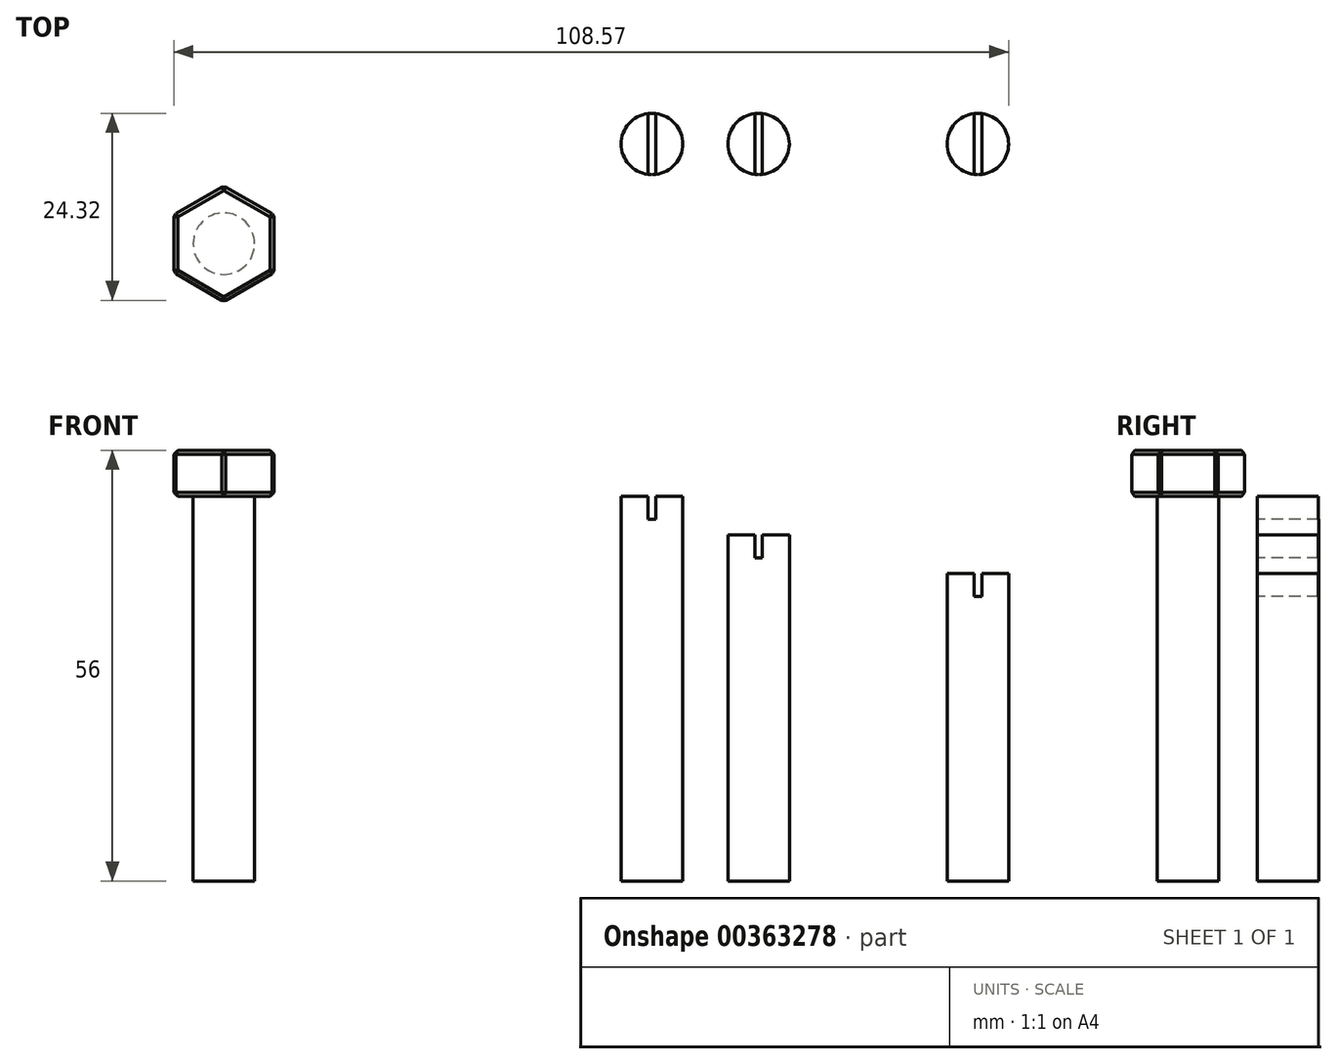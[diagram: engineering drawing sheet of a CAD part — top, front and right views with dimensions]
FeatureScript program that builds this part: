
annotation { "Feature Type Name" : "Feature", "Feature Type Description" : "" }
export const myFeature = defineFeature(function(context is Context, id is Id, definition is map)
    precondition{}
    {
        {
            var Q0;
            Q0=qCreatedBy(makeId("Top.planeOp"),FACE);
            var sketch = newSketch(context, id + "F0", { "sketchPlane" : qUnion([Q0])});
            skCircle(sketch, "E0", {"center": v(0, 0) * mm, "radius": 4 * mm});
            skSolve(sketch);
        }
        {
            var Q0;
            Q0=qSketchRegion(id+"F0",true);
            extrude(context, id + "F1", {"entities" : qUnion([Q0]), "depth" : 50 * mm});
        }
        {
            var Q0;
            Q0=qCreatedBy(makeId("Top.planeOp"),FACE);
            var sketch = newSketch(context, id + "F2", { "sketchPlane" : qUnion([Q0])});
            skCircle(sketch, "E1", {"center": v(42.4, 0) * mm, "radius": 4 * mm});
            skSolve(sketch);
        }
        {
            var Q0;
            Q0=makeQuery(id+"F2.imprint","IMPRINT",FACE,{"disambiguationData":[TD([[makeQuery(id+"F2.imprint","IMPRINT",EDGE,{"derivedFrom":sQuery(id+"F2.wireOp",EDGE,"E1")}),1.0]])]});
            var Q1;
            Q1=sQuery(id+"F2.wireOp",EDGE,"E1");
            extrude(context, id + "F3", {"entities" : qUnion([Q0]), "surfaceEntities" : qUnion([Q1]), "depth" : 40 * mm});
        }
        {
            var Q0;
            Q0=makeQuery(id+"F1.opExtrude","CAP_FACE",FACE,{"disambiguationData":[OSD([sQuery(id+"F0.wireOp",EDGE,"E0")])],"isStart":false});
            var sketch = newSketch(context, id + "F4", { "sketchPlane" : qUnion([Q0])});
            skLineSegment(sketch, "E2.bottom", {"start": v(0.5, 4) * mm, "end": v(-0.5, 4) * mm});
            skLineSegment(sketch, "E2.top", {"start": v(0.5, -4) * mm, "end": v(-0.5, -4) * mm});
            skLineSegment(sketch, "E2.left", {"start": v(0.5, 4) * mm, "end": v(0.5, -4) * mm});
            skLineSegment(sketch, "E2.right", {"start": v(-0.5, 4) * mm, "end": v(-0.5, -4) * mm});
            skPoint(sketch, "E2.middle", {"position": v(0, 0) * mm});
            skSolve(sketch);
        }
        {
            var Q0;
            {var subQ0=makeQuery(id+"F1.opExtrude","CAP_EDGE",EDGE,{"disambiguationData":[OSD([sQuery(id+"F0.wireOp",EDGE,"E0")])],"isStart":false});var subQ4=sQuery(id+"F4.wireOp",EDGE,"E2.left");var subQ5=makeQuery(id+"F4.imprint","INTERSECT",VERTEX,{"disambiguationData":[OD(0.0)],"derivedFrom":[subQ0,subQ4]});Q0=makeQuery(id+"F4.imprint","IMPRINT",FACE,{"disambiguationData":[TD([[makeQuery(id+"F4.imprint","IMPRINT",EDGE,{"disambiguationData":[TD([[subQ5,-1.0]])],"derivedFrom":subQ4}),-1.0]])]});}
            extrude(context, id + "F5", {"entities" : qUnion([Q0]), "operationType" : NewBodyOperationType.REMOVE, "oppositeDirection" : true, "depth" : 3 * mm});
        }
        {
            var Q0;
            Q0=makeQuery(id+"F3.opExtrude","CAP_FACE",FACE,{"disambiguationData":[OSD([sQuery(id+"F2.wireOp",EDGE,"E1")])],"isStart":false});
            var sketch = newSketch(context, id + "F6", { "sketchPlane" : qUnion([Q0])});
            skLineSegment(sketch, "E3.bottom", {"start": v(42.9, 4) * mm, "end": v(41.9, 4) * mm});
            skLineSegment(sketch, "E3.top", {"start": v(42.9, -4) * mm, "end": v(41.9, -4) * mm});
            skLineSegment(sketch, "E3.left", {"start": v(42.9, 4) * mm, "end": v(42.9, -4) * mm});
            skLineSegment(sketch, "E3.right", {"start": v(41.9, 4) * mm, "end": v(41.9, -4) * mm});
            skPoint(sketch, "E3.middle", {"position": v(42.4, 0) * mm});
            skSolve(sketch);
        }
        {
            var Q0;
            {var subQ0=makeQuery(id+"F3.opExtrude","CAP_EDGE",EDGE,{"disambiguationData":[OSD([sQuery(id+"F2.wireOp",EDGE,"E1")])],"isStart":false});var subQ5=sQuery(id+"F6.wireOp",EDGE,"E3.left");var subQ6=makeQuery(id+"F6.imprint","INTERSECT",VERTEX,{"disambiguationData":[OD(0.0)],"derivedFrom":[subQ0,subQ5]});Q0=makeQuery(id+"F6.imprint","IMPRINT",FACE,{"disambiguationData":[TD([[makeQuery(id+"F6.imprint","IMPRINT",EDGE,{"disambiguationData":[TD([[subQ6,-1.0]])],"derivedFrom":subQ5}),-1.0]])]});}
            extrude(context, id + "F7", {"entities" : qUnion([Q0]), "operationType" : NewBodyOperationType.REMOVE, "oppositeDirection" : true, "depth" : 3 * mm});
        }
        {
            var Q0;
            Q0=qCreatedBy(makeId("Top.planeOp"),FACE);
            var sketch = newSketch(context, id + "F8", { "sketchPlane" : qUnion([Q0])});
            skCircle(sketch, "E4", {"center": v(13.88, 0) * mm, "radius": 4 * mm});
            skSolve(sketch);
        }
        {
            var Q0;
            Q0=makeQuery(id+"F8.imprint","IMPRINT",FACE,{"disambiguationData":[TD([[makeQuery(id+"F8.imprint","IMPRINT",EDGE,{"derivedFrom":sQuery(id+"F8.wireOp",EDGE,"E4")}),1.0]])]});
            var Q1;
            Q1=sQuery(id+"F8.wireOp",EDGE,"E4");
            extrude(context, id + "F9", {"entities" : qUnion([Q0]), "surfaceEntities" : qUnion([Q1]), "depth" : 45 * mm});
        }
        {
            var Q0;
            Q0=makeQuery(id+"F9.opExtrude","CAP_FACE",FACE,{"disambiguationData":[OSD([sQuery(id+"F8.wireOp",EDGE,"E4")])],"isStart":false});
            var sketch = newSketch(context, id + "F10", { "sketchPlane" : qUnion([Q0])});
            skLineSegment(sketch, "E5.bottom", {"start": v(14.38, 4) * mm, "end": v(13.38, 4) * mm});
            skLineSegment(sketch, "E5.top", {"start": v(14.38, -4) * mm, "end": v(13.38, -4) * mm});
            skLineSegment(sketch, "E5.left", {"start": v(14.38, 4) * mm, "end": v(14.38, -4) * mm});
            skLineSegment(sketch, "E5.right", {"start": v(13.38, 4) * mm, "end": v(13.38, -4) * mm});
            skPoint(sketch, "E5.middle", {"position": v(13.88, 0) * mm});
            skSolve(sketch);
        }
        {
            var Q0;
            {var subQ0=makeQuery(id+"F9.opExtrude","CAP_EDGE",EDGE,{"disambiguationData":[OSD([sQuery(id+"F8.wireOp",EDGE,"E4")])],"isStart":false});var subQ4=sQuery(id+"F10.wireOp",EDGE,"E5.left");var subQ5=makeQuery(id+"F10.imprint","INTERSECT",VERTEX,{"disambiguationData":[OD(0.0)],"derivedFrom":[subQ0,subQ4]});Q0=makeQuery(id+"F10.imprint","IMPRINT",FACE,{"disambiguationData":[TD([[makeQuery(id+"F10.imprint","IMPRINT",EDGE,{"disambiguationData":[TD([[subQ5,-1.0]])],"derivedFrom":subQ4}),-1.0]])]});}
            extrude(context, id + "F11", {"entities" : qUnion([Q0]), "operationType" : NewBodyOperationType.REMOVE, "oppositeDirection" : true, "depth" : 3 * mm});
        }
        {
            var Q0;
            Q0=qCreatedBy(makeId("Top.planeOp"),FACE);
            var sketch = newSketch(context, id + "F12", { "sketchPlane" : qUnion([Q0])});
            skCircle(sketch, "E6", {"center": v(-55.68, -12.96) * mm, "radius": 4 * mm});
            skSolve(sketch);
        }
        {
            var Q0;
            Q0=makeQuery(id+"F12.imprint","IMPRINT",FACE,{"disambiguationData":[TD([[makeQuery(id+"F12.imprint","IMPRINT",EDGE,{"derivedFrom":sQuery(id+"F12.wireOp",EDGE,"E6")}),1.0]])]});
            extrude(context, id + "F13", {"entities" : qUnion([Q0]), "depth" : 50 * mm});
        }
        {
            var Q0;
            Q0=makeQuery(id+"F13.opExtrude","CAP_FACE",FACE,{"disambiguationData":[OSD([sQuery(id+"F12.wireOp",EDGE,"E6")])],"isStart":false});
            var sketch = newSketch(context, id + "F14", { "sketchPlane" : qUnion([Q0])});
            skCircle(sketch, "E7.cCircle", {"center": v(-55.68, -12.96) * mm, "radius": 6.5 * mm, "construction": true});
            skLineSegment(sketch, "E7.0", {"start": v(-49.18, -9.2) * mm, "end": v(-49.18, -16.72) * mm});
            skLineSegment(sketch, "E7.1", {"start": v(-49.18, -16.72) * mm, "end": v(-55.68, -20.47) * mm});
            skLineSegment(sketch, "E7.2", {"start": v(-55.68, -20.47) * mm, "end": v(-62.18, -16.72) * mm});
            skLineSegment(sketch, "E7.3", {"start": v(-62.18, -16.72) * mm, "end": v(-62.18, -9.2) * mm});
            skLineSegment(sketch, "E7.4", {"start": v(-62.18, -9.2) * mm, "end": v(-55.68, -5.46) * mm});
            skLineSegment(sketch, "E7.5", {"start": v(-55.68, -5.46) * mm, "end": v(-49.18, -9.2) * mm});
            skPoint(sketch, "E7.0.midPoint", {"position": v(-49.18, -12.96) * mm});
            skSolve(sketch);
        }
        {
            var Q0;
            Q0=qSketchRegion(id+"F14",true);
            extrude(context, id + "F15", {"entities" : qUnion([Q0]), "operationType" : NewBodyOperationType.ADD, "depth" : 6 * mm});
        }
        {
            var Q0;
            Q0=makeQuery(id+"F15.opExtrude","CAP_FACE",FACE,{"disambiguationData":[OSD([sQuery(id+"F14.wireOp",EDGE,"E7.0"),sQuery(id+"F14.wireOp",EDGE,"E7.1"),sQuery(id+"F14.wireOp",EDGE,"E7.2"),sQuery(id+"F14.wireOp",EDGE,"E7.3"),sQuery(id+"F14.wireOp",EDGE,"E7.4"),sQuery(id+"F14.wireOp",EDGE,"E7.5")])],"isStart":false});
            var Q1;
            Q1=makeQuery(id+"F15.opExtrude","SWEPT_FACE",FACE,{"disambiguationData":[OSD([sQuery(id+"F14.wireOp",EDGE,"E7.1")])]});
            var Q2;
            Q2=makeQuery(id+"F15.opExtrude","SWEPT_FACE",FACE,{"disambiguationData":[OSD([sQuery(id+"F14.wireOp",EDGE,"E7.2")])]});
            var Q3;
            Q3=makeQuery(id+"F15.opExtrude","SWEPT_FACE",FACE,{"disambiguationData":[OSD([sQuery(id+"F14.wireOp",EDGE,"E7.0")])]});
            var Q4;
            Q4=makeQuery(id+"F15.opExtrude","SWEPT_FACE",FACE,{"disambiguationData":[OSD([sQuery(id+"F14.wireOp",EDGE,"E7.5")])]});
            var Q5;
            Q5=makeQuery(id+"F15.opExtrude","SWEPT_FACE",FACE,{"disambiguationData":[OSD([sQuery(id+"F14.wireOp",EDGE,"E7.4")])]});
            var Q6;
            Q6=makeQuery(id+"F15.opExtrude","SWEPT_FACE",FACE,{"disambiguationData":[OSD([sQuery(id+"F14.wireOp",EDGE,"E7.3")])]});
            chamfer(context, id + "F16", {"entities" : qUnion([Q0, Q1, Q2, Q3, Q4, Q5, Q6]), "width" : .5 * mm, "tangentPropagation" : true});
        }
    });
